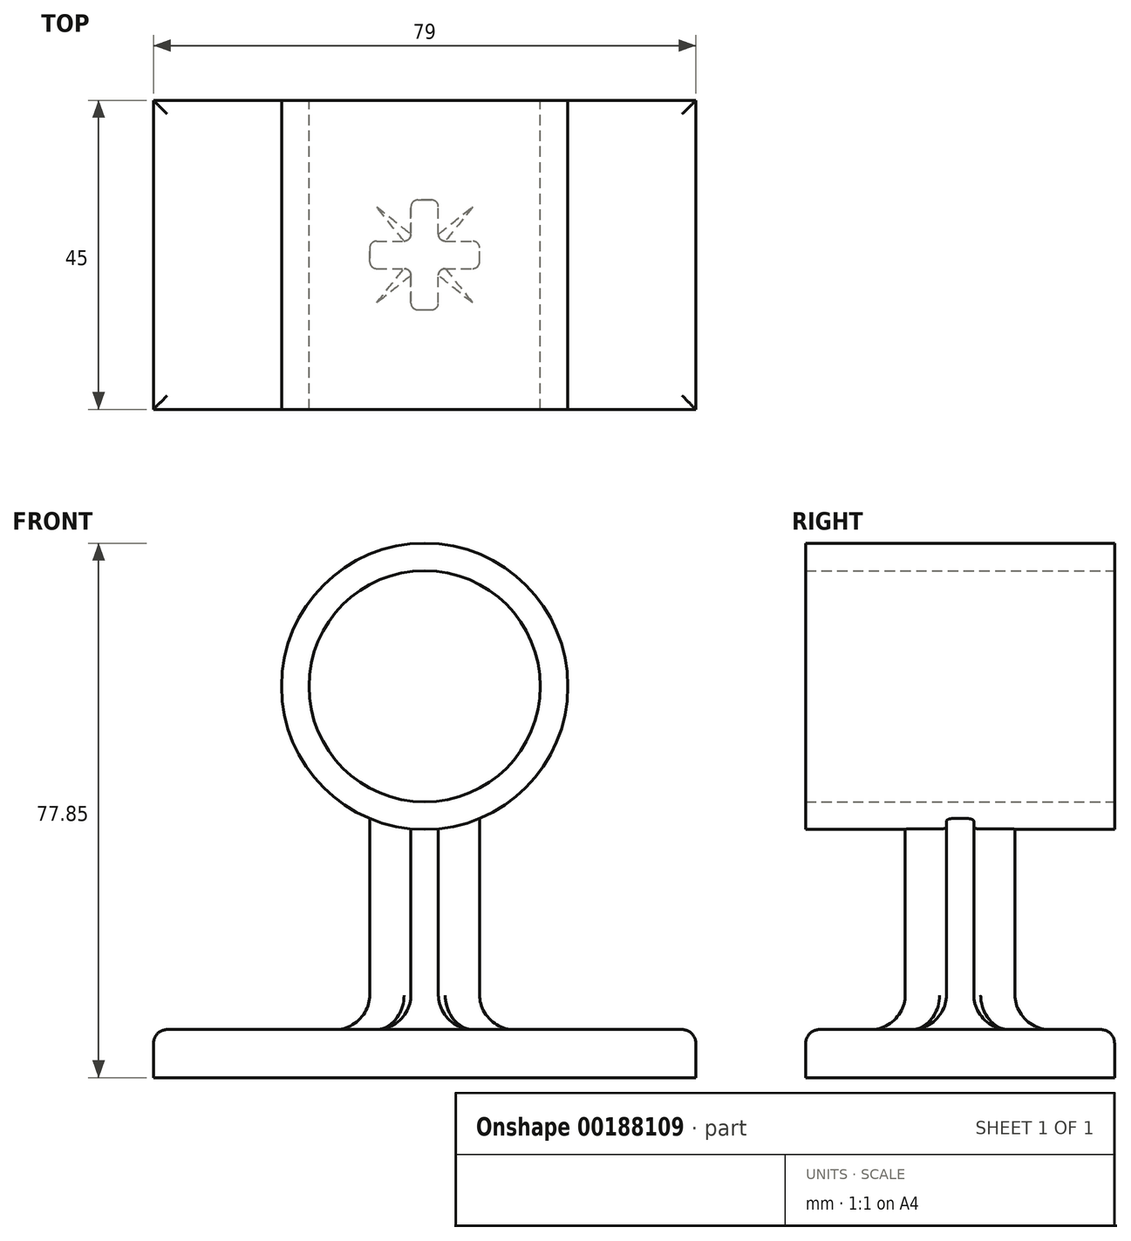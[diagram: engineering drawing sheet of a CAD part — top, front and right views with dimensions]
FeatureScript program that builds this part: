
annotation { "Feature Type Name" : "Feature", "Feature Type Description" : "" }
export const myFeature = defineFeature(function(context is Context, id is Id, definition is map)
    precondition{}
    {
        {
            var Q0;
            Q0=qCreatedBy(makeId("Front.planeOp"),FACE);
            var sketch = newSketch(context, id + "F0", { "sketchPlane" : qUnion([Q0])});
            skLineSegment(sketch, "E0.bottom", {"start": v(0, 0) * mm, "end": v(79, 0) * mm});
            skLineSegment(sketch, "E0.top", {"start": v(0, -7) * mm, "end": v(79, -7) * mm});
            skLineSegment(sketch, "E0.left", {"start": v(0, 0) * mm, "end": v(0, -7) * mm});
            skLineSegment(sketch, "E0.right", {"start": v(79, 0) * mm, "end": v(79, -7) * mm});
            skLineSegment(sketch, "E1", {"start": v(39.5, -7) * mm, "end": v(39.5, 50) * mm});
            skCircle(sketch, "E2", {"center": v(39.5, 50) * mm, "radius": 16.85 * mm});
            skCircle(sketch, "E3", {"center": v(39.5, 50) * mm, "radius": 20.85 * mm});
            skLineSegment(sketch, "E4", {"start": v(39.5, 33.15) * mm, "end": v(39.5, 0) * mm});
            skLineSegment(sketch, "E5.0", {"start": v(31.5, 33.15) * mm, "end": v(31.5, 0) * mm});
            skLineSegment(sketch, "E6.0", {"start": v(47.5, 33.15) * mm, "end": v(47.5, 0) * mm});
            skSolve(sketch);
        }
        {
            var Q0;
            {var subQ0=sQuery(id+"F0.wireOp",EDGE,"E0.left");Q0=makeQuery(id+"F0.imprint","IMPRINT",FACE,{"disambiguationData":[TD([[makeQuery(id+"F0.imprint","IMPRINT",EDGE,{"derivedFrom":subQ0}),1.0]])]});}
            var Q1;
            {var subQ0=sQuery(id+"F0.wireOp",EDGE,"E0.right");Q1=makeQuery(id+"F0.imprint","IMPRINT",FACE,{"disambiguationData":[TD([[makeQuery(id+"F0.imprint","IMPRINT",EDGE,{"derivedFrom":subQ0}),-1.0]])]});}
            var Q2;
            Q2=makeQuery(id+"F0.imprint","IMPRINT",FACE,{"disambiguationData":[TD([[makeQuery(id+"F0.imprint","IMPRINT",EDGE,{"derivedFrom":sQuery(id+"F0.wireOp",EDGE,"E2")}),-1.0]])]});
            extrude(context, id + "F1", {"entities" : qUnion([Q0, Q1, Q2]), "depth" : 45 * mm, "symmetric" : true});
        }
        {
            var Q0;
            {var subQ3=sQuery(id+"F0.wireOp",EDGE,"E5.0");var subQ5=sQuery(id+"F0.wireOp",EDGE,"E3");var subQ6=makeQuery(id+"F0.imprint","INTERSECT",VERTEX,{"derivedFrom":[subQ5,subQ3]});Q0=makeQuery(id+"F0.imprint","IMPRINT",FACE,{"disambiguationData":[TD([[makeQuery(id+"F0.imprint","IMPRINT",EDGE,{"disambiguationData":[TD([[subQ6,-1.0]])],"derivedFrom":subQ5}),-1.0]])]});}
            var Q1;
            {var subQ3=sQuery(id+"F0.wireOp",EDGE,"E6.0");var subQ5=sQuery(id+"F0.wireOp",EDGE,"E3");var subQ6=makeQuery(id+"F0.imprint","INTERSECT",VERTEX,{"derivedFrom":[subQ5,subQ3]});Q1=makeQuery(id+"F0.imprint","IMPRINT",FACE,{"disambiguationData":[TD([[makeQuery(id+"F0.imprint","IMPRINT",EDGE,{"disambiguationData":[TD([[subQ6,1.0]])],"derivedFrom":subQ5}),-1.0]])]});}
            extrude(context, id + "F2", {"entities" : qUnion([Q0, Q1]), "depth" : 4 * mm, "symmetric" : true});
        }
        {
            var Q0;
            Q0=makeQuery(id+"F2.opExtrude","SWEPT_BODY",BODY,{"disambiguationData":[OSD([sQuery(id+"F0.wireOp",EDGE,"E0.bottom"),sQuery(id+"F0.wireOp",EDGE,"E3"),sQuery(id+"F0.wireOp",EDGE,"E5.0"),sQuery(id+"F0.wireOp",EDGE,"E6.0")])]});
            var Q1;
            Q1=sQuery(id+"F0.wireOp",EDGE,"E4");
            transform(context, id + "F3", {"entities" : qUnion([Q0]), "transformType" : TransformType.ROTATION, "transformAxis" : qUnion([Q1]), "angle" : 90 * degree, "makeCopy" : true});
        }
        {
            var Q0;
            Q0=makeQuery(id+"F1.opExtrude","SWEPT_BODY",BODY,{"disambiguationData":[OSD([sQuery(id+"F0.wireOp",EDGE,"E2"),sQuery(id+"F0.wireOp",EDGE,"E3")])]});
            var Q1;
            Q1=makeQuery(id+"F2.opExtrude","SWEPT_BODY",BODY,{"disambiguationData":[OSD([sQuery(id+"F0.wireOp",EDGE,"E0.bottom"),sQuery(id+"F0.wireOp",EDGE,"E3"),sQuery(id+"F0.wireOp",EDGE,"E5.0"),sQuery(id+"F0.wireOp",EDGE,"E6.0")])]});
            var Q2;
            Q2=makeQuery(id+"F1.opExtrude","SWEPT_BODY",BODY,{"disambiguationData":[OSD([sQuery(id+"F0.wireOp",EDGE,"E0.bottom"),sQuery(id+"F0.wireOp",EDGE,"E0.top"),sQuery(id+"F0.wireOp",EDGE,"E0.left"),sQuery(id+"F0.wireOp",EDGE,"E0.right")])]});
            var Q3;
            Q3=makeQuery(id+"F3.opPattern","COPY",BODY,{"derivedFrom":makeQuery(id+"F2.opExtrude","SWEPT_BODY",BODY,{"disambiguationData":[OSD([sQuery(id+"F0.wireOp",EDGE,"E0.bottom"),sQuery(id+"F0.wireOp",EDGE,"E3"),sQuery(id+"F0.wireOp",EDGE,"E5.0"),sQuery(id+"F0.wireOp",EDGE,"E6.0")])]}),"instanceName":"1"});
            booleanBodies(context, id + "F4", {"operationType" : BooleanOperationType.UNION, "tools" : qUnion([Q0, Q1, Q2, Q3])});
        }
        {
            var Q0;
            Q0=makeQuery(id+"F1.opExtrude","SWEPT_EDGE",EDGE,{"disambiguationData":[OSD([sQuery(id+"F0.wireOp",EDGE,"E0.bottom"),sQuery(id+"F0.wireOp",EDGE,"E0.left")])]});
            var Q1;
            Q1=makeQuery(id+"F1.opExtrude","CAP_EDGE",EDGE,{"disambiguationData":[OSD([sQuery(id+"F0.wireOp",EDGE,"E0.bottom")])],"isStart":true});
            var Q2;
            Q2=makeQuery(id+"F1.opExtrude","SWEPT_EDGE",EDGE,{"disambiguationData":[OSD([sQuery(id+"F0.wireOp",EDGE,"E0.bottom"),sQuery(id+"F0.wireOp",EDGE,"E0.right")])]});
            var Q3;
            Q3=makeQuery(id+"F1.opExtrude","CAP_EDGE",EDGE,{"disambiguationData":[OSD([sQuery(id+"F0.wireOp",EDGE,"E0.bottom")])],"isStart":false});
            fillet(context, id + "F5", {"entities" : qUnion([Q0, Q1, Q2, Q3]), "radius" : 2 * mm, "tangentPropagation" : true, "allowEdgeOverflow" : false});
        }
        {
            var Q0;
            Q0=makeQuery(id+"F3.opPattern","COPY",EDGE,{"derivedFrom":makeQuery(id+"F2.opExtrude","CAP_EDGE",EDGE,{"disambiguationData":[OSD([sQuery(id+"F0.wireOp",EDGE,"E6.0")])],"isStart":true}),"instanceName":"1"});
            var Q1;
            Q1=makeQuery(id+"F2.opExtrude","CAP_EDGE",EDGE,{"disambiguationData":[OSD([sQuery(id+"F0.wireOp",EDGE,"E6.0")])],"isStart":false});
            var Q2;
            Q2=makeQuery(id+"F2.opExtrude","CAP_EDGE",EDGE,{"disambiguationData":[OSD([sQuery(id+"F0.wireOp",EDGE,"E6.0")])],"isStart":true});
            var Q3;
            {var subQ0=makeQuery(id+"F2.opExtrude","CAP_FACE",FACE,{"disambiguationData":[OSD([sQuery(id+"F0.wireOp",EDGE,"E0.bottom"),sQuery(id+"F0.wireOp",EDGE,"E3"),sQuery(id+"F0.wireOp",EDGE,"E5.0"),sQuery(id+"F0.wireOp",EDGE,"E6.0")])],"isStart":true});Q3=makeQuery(id+"F4.opBoolean","INTERSECT",EDGE,{"derivedFrom":[subQ0,makeQuery(id+"F3.opPattern","COPY",FACE,{"derivedFrom":subQ0,"instanceName":"1"})]});}
            var Q4;
            Q4=makeQuery(id+"F3.opPattern","COPY",EDGE,{"derivedFrom":makeQuery(id+"F2.opExtrude","CAP_EDGE",EDGE,{"disambiguationData":[OSD([sQuery(id+"F0.wireOp",EDGE,"E5.0")])],"isStart":true}),"instanceName":"1"});
            var Q5;
            Q5=makeQuery(id+"F3.opPattern","COPY",EDGE,{"derivedFrom":makeQuery(id+"F2.opExtrude","CAP_EDGE",EDGE,{"disambiguationData":[OSD([sQuery(id+"F0.wireOp",EDGE,"E5.0")])],"isStart":false}),"instanceName":"1"});
            var Q6;
            {var subQ0=sQuery(id+"F0.wireOp",EDGE,"E6.0");var subQ1=sQuery(id+"F0.wireOp",EDGE,"E5.0");var subQ2=sQuery(id+"F0.wireOp",EDGE,"E3");var subQ3=sQuery(id+"F0.wireOp",EDGE,"E0.bottom");Q6=makeQuery(id+"F4.opBoolean","INTERSECT",EDGE,{"derivedFrom":[makeQuery(id+"F2.opExtrude","CAP_FACE",FACE,{"disambiguationData":[OSD([subQ3,subQ2,subQ1,subQ0])],"isStart":false}),makeQuery(id+"F3.opPattern","COPY",FACE,{"derivedFrom":makeQuery(id+"F2.opExtrude","CAP_FACE",FACE,{"disambiguationData":[OSD([subQ3,subQ2,subQ1,subQ0])],"isStart":true}),"instanceName":"1"})]});}
            var Q7;
            {var subQ0=makeQuery(id+"F2.opExtrude","CAP_FACE",FACE,{"disambiguationData":[OSD([sQuery(id+"F0.wireOp",EDGE,"E0.bottom"),sQuery(id+"F0.wireOp",EDGE,"E3"),sQuery(id+"F0.wireOp",EDGE,"E5.0"),sQuery(id+"F0.wireOp",EDGE,"E6.0")])],"isStart":false});Q7=makeQuery(id+"F4.opBoolean","INTERSECT",EDGE,{"derivedFrom":[subQ0,makeQuery(id+"F3.opPattern","COPY",FACE,{"derivedFrom":subQ0,"instanceName":"1"})]});}
            var Q8;
            Q8=makeQuery(id+"F2.opExtrude","CAP_EDGE",EDGE,{"disambiguationData":[OSD([sQuery(id+"F0.wireOp",EDGE,"E5.0")])],"isStart":false});
            var Q9;
            Q9=makeQuery(id+"F2.opExtrude","CAP_EDGE",EDGE,{"disambiguationData":[OSD([sQuery(id+"F0.wireOp",EDGE,"E5.0")])],"isStart":true});
            var Q10;
            Q10=makeQuery(id+"F3.opPattern","COPY",EDGE,{"derivedFrom":makeQuery(id+"F2.opExtrude","CAP_EDGE",EDGE,{"disambiguationData":[OSD([sQuery(id+"F0.wireOp",EDGE,"E6.0")])],"isStart":false}),"instanceName":"1"});
            var Q11;
            {var subQ0=sQuery(id+"F0.wireOp",EDGE,"E6.0");var subQ1=sQuery(id+"F0.wireOp",EDGE,"E5.0");var subQ2=sQuery(id+"F0.wireOp",EDGE,"E3");var subQ3=sQuery(id+"F0.wireOp",EDGE,"E0.bottom");Q11=makeQuery(id+"F4.opBoolean","INTERSECT",EDGE,{"derivedFrom":[makeQuery(id+"F2.opExtrude","CAP_FACE",FACE,{"disambiguationData":[OSD([subQ3,subQ2,subQ1,subQ0])],"isStart":true}),makeQuery(id+"F3.opPattern","COPY",FACE,{"derivedFrom":makeQuery(id+"F2.opExtrude","CAP_FACE",FACE,{"disambiguationData":[OSD([subQ3,subQ2,subQ1,subQ0])],"isStart":false}),"instanceName":"1"})]});}
            fillet(context, id + "F6", {"entities" : qUnion([Q0, Q1, Q2, Q3, Q4, Q5, Q6, Q7, Q8, Q9, Q10, Q11]), "radius" : 1 * mm, "tangentPropagation" : true, "allowEdgeOverflow" : false});
        }
        {
            var Q0;
            {var subQ0=sQuery(id+"F0.wireOp",EDGE,"E0.bottom");var subQ1=sQuery(id+"F0.wireOp",EDGE,"E6.0");Q0=makeQuery(id+"F4.opBoolean","SPLIT",EDGE,{"disambiguationData":[TD([makeQuery(id+"F3.opPattern","COPY",FACE,{"derivedFrom":makeQuery(id+"F2.opExtrude","SWEPT_FACE",FACE,{"disambiguationData":[OSD([subQ1])]}),"instanceName":"1"})])],"derivedFrom":makeQuery(id+"F3.opPattern","COPY",EDGE,{"derivedFrom":makeQuery(id+"F2.opExtrude","CAP_EDGE",EDGE,{"disambiguationData":[OSD([subQ0])],"isStart":true}),"instanceName":"1"})});}
            var Q1;
            {var subQ0=sQuery(id+"F0.wireOp",EDGE,"E0.bottom");var subQ1=sQuery(id+"F0.wireOp",EDGE,"E6.0");var subQ2=sQuery(id+"F0.wireOp",EDGE,"E5.0");var subQ3=sQuery(id+"F0.wireOp",EDGE,"E3");Q1=makeQuery(id+"F6.opFillet","BLEND_EDGE",EDGE,{"blendedFrom":[makeQuery(id+"F4.opBoolean","INTERSECT",EDGE,{"derivedFrom":[makeQuery(id+"F2.opExtrude","CAP_FACE",FACE,{"disambiguationData":[OSD([subQ0,subQ3,subQ2,subQ1])],"isStart":false}),makeQuery(id+"F3.opPattern","COPY",FACE,{"derivedFrom":makeQuery(id+"F2.opExtrude","CAP_FACE",FACE,{"disambiguationData":[OSD([subQ0,subQ3,subQ2,subQ1])],"isStart":true}),"instanceName":"1"})]}),makeQuery(id+"F1.opExtrude","SWEPT_FACE",FACE,{"disambiguationData":[OSD([subQ0])]})],"blendedInto":[makeQuery(id+"F1.opExtrude","SWEPT_FACE",FACE,{"disambiguationData":[OSD([subQ0])]})]});}
            var Q2;
            {var subQ0=sQuery(id+"F0.wireOp",EDGE,"E0.bottom");var subQ1=sQuery(id+"F0.wireOp",EDGE,"E6.0");Q2=makeQuery(id+"F4.opBoolean","SPLIT",EDGE,{"disambiguationData":[TD([makeQuery(id+"F2.opExtrude","SWEPT_FACE",FACE,{"disambiguationData":[OSD([subQ1])]})])],"derivedFrom":makeQuery(id+"F2.opExtrude","CAP_EDGE",EDGE,{"disambiguationData":[OSD([subQ0])],"isStart":false})});}
            var Q3;
            Q3=makeQuery(id+"F6.opFillet","BLEND_EDGE",EDGE,{"blendedFrom":[makeQuery(id+"F2.opExtrude","CAP_EDGE",EDGE,{"disambiguationData":[OSD([sQuery(id+"F0.wireOp",EDGE,"E6.0")])],"isStart":false}),makeQuery(id+"F1.opExtrude","SWEPT_FACE",FACE,{"disambiguationData":[OSD([sQuery(id+"F0.wireOp",EDGE,"E0.bottom")])]})],"blendedInto":[makeQuery(id+"F1.opExtrude","SWEPT_FACE",FACE,{"disambiguationData":[OSD([sQuery(id+"F0.wireOp",EDGE,"E0.bottom")])]})]});
            var Q4;
            Q4=makeQuery(id+"F2.opExtrude","SWEPT_EDGE",EDGE,{"disambiguationData":[OSD([sQuery(id+"F0.wireOp",EDGE,"E0.bottom"),sQuery(id+"F0.wireOp",EDGE,"E6.0")])]});
            var Q5;
            Q5=makeQuery(id+"F6.opFillet","BLEND_EDGE",EDGE,{"blendedFrom":[makeQuery(id+"F2.opExtrude","CAP_EDGE",EDGE,{"disambiguationData":[OSD([sQuery(id+"F0.wireOp",EDGE,"E6.0")])],"isStart":true}),makeQuery(id+"F1.opExtrude","SWEPT_FACE",FACE,{"disambiguationData":[OSD([sQuery(id+"F0.wireOp",EDGE,"E0.bottom")])]})],"blendedInto":[makeQuery(id+"F1.opExtrude","SWEPT_FACE",FACE,{"disambiguationData":[OSD([sQuery(id+"F0.wireOp",EDGE,"E0.bottom")])]})]});
            var Q6;
            {var subQ0=sQuery(id+"F0.wireOp",EDGE,"E0.bottom");var subQ1=sQuery(id+"F0.wireOp",EDGE,"E6.0");Q6=makeQuery(id+"F4.opBoolean","SPLIT",EDGE,{"disambiguationData":[TD([makeQuery(id+"F2.opExtrude","SWEPT_FACE",FACE,{"disambiguationData":[OSD([subQ1])]})])],"derivedFrom":makeQuery(id+"F2.opExtrude","CAP_EDGE",EDGE,{"disambiguationData":[OSD([subQ0])],"isStart":true})});}
            var Q7;
            {var subQ0=sQuery(id+"F0.wireOp",EDGE,"E0.bottom");var subQ1=makeQuery(id+"F2.opExtrude","CAP_FACE",FACE,{"disambiguationData":[OSD([subQ0,sQuery(id+"F0.wireOp",EDGE,"E3"),sQuery(id+"F0.wireOp",EDGE,"E5.0"),sQuery(id+"F0.wireOp",EDGE,"E6.0")])],"isStart":true});Q7=makeQuery(id+"F6.opFillet","BLEND_EDGE",EDGE,{"blendedFrom":[makeQuery(id+"F4.opBoolean","INTERSECT",EDGE,{"derivedFrom":[subQ1,makeQuery(id+"F3.opPattern","COPY",FACE,{"derivedFrom":subQ1,"instanceName":"1"})]}),makeQuery(id+"F1.opExtrude","SWEPT_FACE",FACE,{"disambiguationData":[OSD([subQ0])]})],"blendedInto":[makeQuery(id+"F1.opExtrude","SWEPT_FACE",FACE,{"disambiguationData":[OSD([subQ0])]})]});}
            var Q8;
            {var subQ0=sQuery(id+"F0.wireOp",EDGE,"E0.bottom");var subQ1=sQuery(id+"F0.wireOp",EDGE,"E5.0");Q8=makeQuery(id+"F4.opBoolean","SPLIT",EDGE,{"disambiguationData":[TD([makeQuery(id+"F3.opPattern","COPY",FACE,{"derivedFrom":makeQuery(id+"F2.opExtrude","SWEPT_FACE",FACE,{"disambiguationData":[OSD([subQ1])]}),"instanceName":"1"})])],"derivedFrom":makeQuery(id+"F3.opPattern","COPY",EDGE,{"derivedFrom":makeQuery(id+"F2.opExtrude","CAP_EDGE",EDGE,{"disambiguationData":[OSD([subQ0])],"isStart":true}),"instanceName":"1"})});}
            var Q9;
            Q9=makeQuery(id+"F6.opFillet","BLEND_EDGE",EDGE,{"blendedFrom":[makeQuery(id+"F3.opPattern","COPY",EDGE,{"derivedFrom":makeQuery(id+"F2.opExtrude","CAP_EDGE",EDGE,{"disambiguationData":[OSD([sQuery(id+"F0.wireOp",EDGE,"E5.0")])],"isStart":true}),"instanceName":"1"}),makeQuery(id+"F1.opExtrude","SWEPT_FACE",FACE,{"disambiguationData":[OSD([sQuery(id+"F0.wireOp",EDGE,"E0.bottom")])]})],"blendedInto":[makeQuery(id+"F1.opExtrude","SWEPT_FACE",FACE,{"disambiguationData":[OSD([sQuery(id+"F0.wireOp",EDGE,"E0.bottom")])]})]});
            var Q10;
            Q10=makeQuery(id+"F3.opPattern","COPY",EDGE,{"derivedFrom":makeQuery(id+"F2.opExtrude","SWEPT_EDGE",EDGE,{"disambiguationData":[OSD([sQuery(id+"F0.wireOp",EDGE,"E0.bottom"),sQuery(id+"F0.wireOp",EDGE,"E5.0")])]}),"instanceName":"1"});
            var Q11;
            Q11=makeQuery(id+"F6.opFillet","BLEND_EDGE",EDGE,{"blendedFrom":[makeQuery(id+"F3.opPattern","COPY",EDGE,{"derivedFrom":makeQuery(id+"F2.opExtrude","CAP_EDGE",EDGE,{"disambiguationData":[OSD([sQuery(id+"F0.wireOp",EDGE,"E5.0")])],"isStart":false}),"instanceName":"1"}),makeQuery(id+"F1.opExtrude","SWEPT_FACE",FACE,{"disambiguationData":[OSD([sQuery(id+"F0.wireOp",EDGE,"E0.bottom")])]})],"blendedInto":[makeQuery(id+"F1.opExtrude","SWEPT_FACE",FACE,{"disambiguationData":[OSD([sQuery(id+"F0.wireOp",EDGE,"E0.bottom")])]})]});
            var Q12;
            {var subQ0=sQuery(id+"F0.wireOp",EDGE,"E0.bottom");var subQ2=sQuery(id+"F0.wireOp",EDGE,"E5.0");Q12=makeQuery(id+"F4.opBoolean","SPLIT",EDGE,{"disambiguationData":[TD([makeQuery(id+"F3.opPattern","COPY",FACE,{"derivedFrom":makeQuery(id+"F2.opExtrude","SWEPT_FACE",FACE,{"disambiguationData":[OSD([subQ2])]}),"instanceName":"1"})])],"derivedFrom":makeQuery(id+"F3.opPattern","COPY",EDGE,{"derivedFrom":makeQuery(id+"F2.opExtrude","CAP_EDGE",EDGE,{"disambiguationData":[OSD([subQ0])],"isStart":false}),"instanceName":"1"})});}
            var Q13;
            {var subQ0=sQuery(id+"F0.wireOp",EDGE,"E0.bottom");var subQ1=sQuery(id+"F0.wireOp",EDGE,"E6.0");var subQ2=sQuery(id+"F0.wireOp",EDGE,"E5.0");var subQ3=sQuery(id+"F0.wireOp",EDGE,"E3");Q13=makeQuery(id+"F6.opFillet","BLEND_EDGE",EDGE,{"blendedFrom":[makeQuery(id+"F4.opBoolean","INTERSECT",EDGE,{"derivedFrom":[makeQuery(id+"F2.opExtrude","CAP_FACE",FACE,{"disambiguationData":[OSD([subQ0,subQ3,subQ2,subQ1])],"isStart":true}),makeQuery(id+"F3.opPattern","COPY",FACE,{"derivedFrom":makeQuery(id+"F2.opExtrude","CAP_FACE",FACE,{"disambiguationData":[OSD([subQ0,subQ3,subQ2,subQ1])],"isStart":false}),"instanceName":"1"})]}),makeQuery(id+"F1.opExtrude","SWEPT_FACE",FACE,{"disambiguationData":[OSD([subQ0])]})],"blendedInto":[makeQuery(id+"F1.opExtrude","SWEPT_FACE",FACE,{"disambiguationData":[OSD([subQ0])]})]});}
            var Q14;
            {var subQ0=sQuery(id+"F0.wireOp",EDGE,"E0.bottom");var subQ1=sQuery(id+"F0.wireOp",EDGE,"E5.0");Q14=makeQuery(id+"F4.opBoolean","SPLIT",EDGE,{"disambiguationData":[TD([makeQuery(id+"F2.opExtrude","SWEPT_FACE",FACE,{"disambiguationData":[OSD([subQ1])]})])],"derivedFrom":makeQuery(id+"F2.opExtrude","CAP_EDGE",EDGE,{"disambiguationData":[OSD([subQ0])],"isStart":true})});}
            var Q15;
            Q15=makeQuery(id+"F6.opFillet","BLEND_EDGE",EDGE,{"blendedFrom":[makeQuery(id+"F2.opExtrude","CAP_EDGE",EDGE,{"disambiguationData":[OSD([sQuery(id+"F0.wireOp",EDGE,"E5.0")])],"isStart":true}),makeQuery(id+"F1.opExtrude","SWEPT_FACE",FACE,{"disambiguationData":[OSD([sQuery(id+"F0.wireOp",EDGE,"E0.bottom")])]})],"blendedInto":[makeQuery(id+"F1.opExtrude","SWEPT_FACE",FACE,{"disambiguationData":[OSD([sQuery(id+"F0.wireOp",EDGE,"E0.bottom")])]})]});
            var Q16;
            Q16=makeQuery(id+"F2.opExtrude","SWEPT_EDGE",EDGE,{"disambiguationData":[OSD([sQuery(id+"F0.wireOp",EDGE,"E0.bottom"),sQuery(id+"F0.wireOp",EDGE,"E5.0")])]});
            var Q17;
            Q17=makeQuery(id+"F6.opFillet","BLEND_EDGE",EDGE,{"blendedFrom":[makeQuery(id+"F2.opExtrude","CAP_EDGE",EDGE,{"disambiguationData":[OSD([sQuery(id+"F0.wireOp",EDGE,"E5.0")])],"isStart":false}),makeQuery(id+"F1.opExtrude","SWEPT_FACE",FACE,{"disambiguationData":[OSD([sQuery(id+"F0.wireOp",EDGE,"E0.bottom")])]})],"blendedInto":[makeQuery(id+"F1.opExtrude","SWEPT_FACE",FACE,{"disambiguationData":[OSD([sQuery(id+"F0.wireOp",EDGE,"E0.bottom")])]})]});
            var Q18;
            {var subQ0=sQuery(id+"F0.wireOp",EDGE,"E0.bottom");var subQ1=sQuery(id+"F0.wireOp",EDGE,"E5.0");Q18=makeQuery(id+"F4.opBoolean","SPLIT",EDGE,{"disambiguationData":[TD([makeQuery(id+"F2.opExtrude","SWEPT_FACE",FACE,{"disambiguationData":[OSD([subQ1])]})])],"derivedFrom":makeQuery(id+"F2.opExtrude","CAP_EDGE",EDGE,{"disambiguationData":[OSD([subQ0])],"isStart":false})});}
            var Q19;
            {var subQ0=sQuery(id+"F0.wireOp",EDGE,"E0.bottom");var subQ1=makeQuery(id+"F2.opExtrude","CAP_FACE",FACE,{"disambiguationData":[OSD([subQ0,sQuery(id+"F0.wireOp",EDGE,"E3"),sQuery(id+"F0.wireOp",EDGE,"E5.0"),sQuery(id+"F0.wireOp",EDGE,"E6.0")])],"isStart":false});Q19=makeQuery(id+"F6.opFillet","BLEND_EDGE",EDGE,{"blendedFrom":[makeQuery(id+"F4.opBoolean","INTERSECT",EDGE,{"derivedFrom":[subQ1,makeQuery(id+"F3.opPattern","COPY",FACE,{"derivedFrom":subQ1,"instanceName":"1"})]}),makeQuery(id+"F1.opExtrude","SWEPT_FACE",FACE,{"disambiguationData":[OSD([subQ0])]})],"blendedInto":[makeQuery(id+"F1.opExtrude","SWEPT_FACE",FACE,{"disambiguationData":[OSD([subQ0])]})]});}
            var Q20;
            {var subQ0=sQuery(id+"F0.wireOp",EDGE,"E0.bottom");var subQ1=sQuery(id+"F0.wireOp",EDGE,"E6.0");Q20=makeQuery(id+"F4.opBoolean","SPLIT",EDGE,{"disambiguationData":[TD([makeQuery(id+"F3.opPattern","COPY",FACE,{"derivedFrom":makeQuery(id+"F2.opExtrude","SWEPT_FACE",FACE,{"disambiguationData":[OSD([subQ1])]}),"instanceName":"1"})])],"derivedFrom":makeQuery(id+"F3.opPattern","COPY",EDGE,{"derivedFrom":makeQuery(id+"F2.opExtrude","CAP_EDGE",EDGE,{"disambiguationData":[OSD([subQ0])],"isStart":false}),"instanceName":"1"})});}
            var Q21;
            Q21=makeQuery(id+"F6.opFillet","BLEND_EDGE",EDGE,{"blendedFrom":[makeQuery(id+"F3.opPattern","COPY",EDGE,{"derivedFrom":makeQuery(id+"F2.opExtrude","CAP_EDGE",EDGE,{"disambiguationData":[OSD([sQuery(id+"F0.wireOp",EDGE,"E6.0")])],"isStart":false}),"instanceName":"1"}),makeQuery(id+"F1.opExtrude","SWEPT_FACE",FACE,{"disambiguationData":[OSD([sQuery(id+"F0.wireOp",EDGE,"E0.bottom")])]})],"blendedInto":[makeQuery(id+"F1.opExtrude","SWEPT_FACE",FACE,{"disambiguationData":[OSD([sQuery(id+"F0.wireOp",EDGE,"E0.bottom")])]})]});
            var Q22;
            Q22=makeQuery(id+"F3.opPattern","COPY",EDGE,{"derivedFrom":makeQuery(id+"F2.opExtrude","SWEPT_EDGE",EDGE,{"disambiguationData":[OSD([sQuery(id+"F0.wireOp",EDGE,"E0.bottom"),sQuery(id+"F0.wireOp",EDGE,"E6.0")])]}),"instanceName":"1"});
            var Q23;
            Q23=makeQuery(id+"F6.opFillet","BLEND_EDGE",EDGE,{"blendedFrom":[makeQuery(id+"F3.opPattern","COPY",EDGE,{"derivedFrom":makeQuery(id+"F2.opExtrude","CAP_EDGE",EDGE,{"disambiguationData":[OSD([sQuery(id+"F0.wireOp",EDGE,"E6.0")])],"isStart":true}),"instanceName":"1"}),makeQuery(id+"F1.opExtrude","SWEPT_FACE",FACE,{"disambiguationData":[OSD([sQuery(id+"F0.wireOp",EDGE,"E0.bottom")])]})],"blendedInto":[makeQuery(id+"F1.opExtrude","SWEPT_FACE",FACE,{"disambiguationData":[OSD([sQuery(id+"F0.wireOp",EDGE,"E0.bottom")])]})]});
            fillet(context, id + "F7", {"entities" : qUnion([Q0, Q1, Q2, Q3, Q4, Q5, Q6, Q7, Q8, Q9, Q10, Q11, Q12, Q13, Q14, Q15, Q16, Q17, Q18, Q19, Q20, Q21, Q22, Q23]), "radius" : 5 * mm, "tangentPropagation" : true, "rho" : 0.4, "crossSection" : FilletCrossSection.CONIC, "allowEdgeOverflow" : false});
        }
    });
